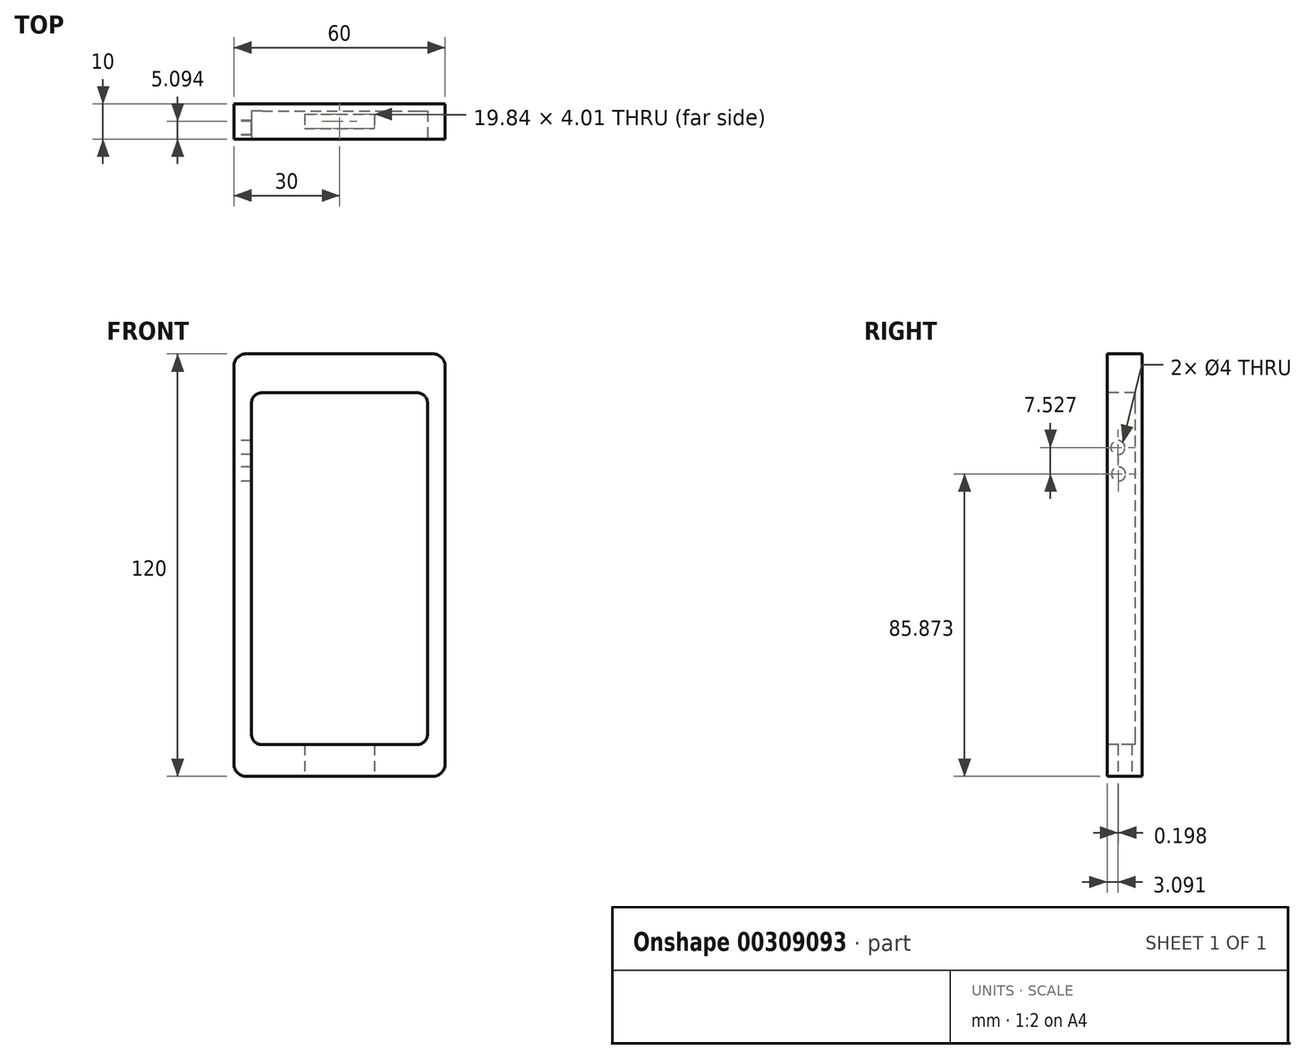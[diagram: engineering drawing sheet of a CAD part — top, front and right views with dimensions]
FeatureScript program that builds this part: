
annotation { "Feature Type Name" : "Feature", "Feature Type Description" : "" }
export const myFeature = defineFeature(function(context is Context, id is Id, definition is map)
    precondition{}
    {
        {
            var Q0;
            Q0=qCreatedBy(makeId("Front.planeOp"),FACE);
            var sketch = newSketch(context, id + "F0", { "sketchPlane" : qUnion([Q0])});
            skLineSegment(sketch, "E0.bottom", {"start": v(-26.5, 60) * mm, "end": v(26.5, 60) * mm});
            skLineSegment(sketch, "E0.top", {"start": v(-26.5, -60) * mm, "end": v(26.5, -60) * mm});
            skLineSegment(sketch, "E0.left", {"start": v(-30, 56.5) * mm, "end": v(-30, -56.5) * mm});
            skLineSegment(sketch, "E0.right", {"start": v(30, 56.5) * mm, "end": v(30, -56.5) * mm});
            skPoint(sketch, "E0.middle", {"position": v(0, 0) * mm});
            skPoint(sketch, "E1.visualSharp", {"position": v(-30, 60) * mm});
            skArc(sketch, "E1.filletArc", {"start": v(-26.5, 60) * mm, "mid": v(-28.97, 58.97) * mm, "end": v(-30, 56.5) * mm});
            skPoint(sketch, "E2.visualSharp", {"position": v(30, 60) * mm});
            skArc(sketch, "E2.filletArc", {"start": v(30, 56.5) * mm, "mid": v(28.97, 58.97) * mm, "end": v(26.5, 60) * mm});
            skPoint(sketch, "E3.visualSharp", {"position": v(30, -60) * mm});
            skArc(sketch, "E3.filletArc", {"start": v(26.5, -60) * mm, "mid": v(28.97, -58.97) * mm, "end": v(30, -56.5) * mm});
            skPoint(sketch, "E4.visualSharp", {"position": v(-30, -60) * mm});
            skArc(sketch, "E4.filletArc", {"start": v(-30, -56.5) * mm, "mid": v(-28.97, -58.97) * mm, "end": v(-26.5, -60) * mm});
            skSolve(sketch);
        }
        {
            var Q0;
            Q0=makeQuery(id+"F0.imprint","IMPRINT",FACE,{"disambiguationData":[TD([[makeQuery(id+"F0.imprint","IMPRINT",EDGE,{"derivedFrom":sQuery(id+"F0.wireOp",EDGE,"E0.bottom")}),-1.0]])]});
            extrude(context, id + "F1", {"entities" : qUnion([Q0]), "depth" : 10 * mm});
        }
        {
            var Q0;
            Q0=makeQuery(id+"F1.opExtrude","CAP_FACE",FACE,{"disambiguationData":[OSD([sQuery(id+"F0.wireOp",EDGE,"E0.bottom"),sQuery(id+"F0.wireOp",EDGE,"E0.top"),sQuery(id+"F0.wireOp",EDGE,"E0.left"),sQuery(id+"F0.wireOp",EDGE,"E0.right"),sQuery(id+"F0.wireOp",EDGE,"E1.filletArc"),sQuery(id+"F0.wireOp",EDGE,"E2.filletArc"),sQuery(id+"F0.wireOp",EDGE,"E3.filletArc"),sQuery(id+"F0.wireOp",EDGE,"E4.filletArc")])],"isStart":false});
            var sketch = newSketch(context, id + "F2", { "sketchPlane" : qUnion([Q0])});
            skLineSegment(sketch, "E5.bottom", {"start": v(-22, 48.97) * mm, "end": v(22, 48.97) * mm});
            skLineSegment(sketch, "E5.top", {"start": v(-22, -51.03) * mm, "end": v(22, -51.03) * mm});
            skLineSegment(sketch, "E5.left", {"start": v(-25, 45.97) * mm, "end": v(-25, -48.03) * mm});
            skLineSegment(sketch, "E5.right", {"start": v(25, 45.97) * mm, "end": v(25, -48.03) * mm});
            skPoint(sketch, "E6.visualSharp", {"position": v(-25, 48.97) * mm});
            skArc(sketch, "E6.filletArc", {"start": v(-22, 48.97) * mm, "mid": v(-24.12, 48.1) * mm, "end": v(-25, 45.97) * mm});
            skPoint(sketch, "E7.visualSharp", {"position": v(25, 48.97) * mm});
            skArc(sketch, "E7.filletArc", {"start": v(25, 45.97) * mm, "mid": v(24.12, 48.1) * mm, "end": v(22, 48.97) * mm});
            skPoint(sketch, "E8.visualSharp", {"position": v(-25, -51.03) * mm});
            skArc(sketch, "E8.filletArc", {"start": v(-25, -48.03) * mm, "mid": v(-24.12, -50.15) * mm, "end": v(-22, -51.03) * mm});
            skPoint(sketch, "E9.visualSharp", {"position": v(25, -51.03) * mm});
            skArc(sketch, "E9.filletArc", {"start": v(22, -51.03) * mm, "mid": v(24.12, -50.15) * mm, "end": v(25, -48.03) * mm});
            skSolve(sketch);
        }
        {
            var Q0;
            Q0 = qSketchRegion(id + "F2", true);
            extrude(context, id + "F3", {"entities" : qUnion([Q0]), "operationType" : NewBodyOperationType.REMOVE, "oppositeDirection" : true, "depth" : 8 * mm});
        }
        {
            var Q0;
            Q0=makeQuery(id+"F1.opExtrude","SWEPT_FACE",FACE,{"disambiguationData":[OSD([sQuery(id+"F0.wireOp",EDGE,"E0.top")])]});
            var sketch = newSketch(context, id + "F4", { "sketchPlane" : qUnion([Q0])});
            skLineSegment(sketch, "E10.bottom", {"start": v(-9.92, 2.9) * mm, "end": v(9.92, 2.9) * mm});
            skLineSegment(sketch, "E10.top", {"start": v(-9.92, 6.91) * mm, "end": v(9.92, 6.91) * mm});
            skLineSegment(sketch, "E10.left", {"start": v(-9.92, 2.9) * mm, "end": v(-9.92, 6.91) * mm});
            skLineSegment(sketch, "E10.right", {"start": v(9.92, 2.9) * mm, "end": v(9.92, 6.91) * mm});
            skPoint(sketch, "E10.middle", {"position": v(0, 4.9) * mm});
            skSolve(sketch);
        }
        {
            var Q0;
            Q0 = qSketchRegion(id + "F4", true);
            extrude(context, id + "F5", {"entities" : qUnion([Q0]), "operationType" : NewBodyOperationType.REMOVE, "oppositeDirection" : true, "depth" : 10 * mm});
        }
        {
            var Q0;
            Q0=makeQuery(id+"F1.opExtrude","SWEPT_FACE",FACE,{"disambiguationData":[OSD([sQuery(id+"F0.wireOp",EDGE,"E0.left")])]});
            var sketch = newSketch(context, id + "F6", { "sketchPlane" : qUnion([Q0])});
            skCircle(sketch, "E11", {"center": v(6.9, 33.4) * mm, "radius": 2 * mm});
            skCircle(sketch, "E12", {"center": v(6.71, 25.87) * mm, "radius": 2 * mm});
            skSolve(sketch);
        }
        {
            var Q0;
            Q0 = qSketchRegion(id + "F6", true);
            extrude(context, id + "F7", {"entities" : qUnion([Q0]), "operationType" : NewBodyOperationType.REMOVE, "oppositeDirection" : true, "depth" : 5 * mm});
        }
    });
